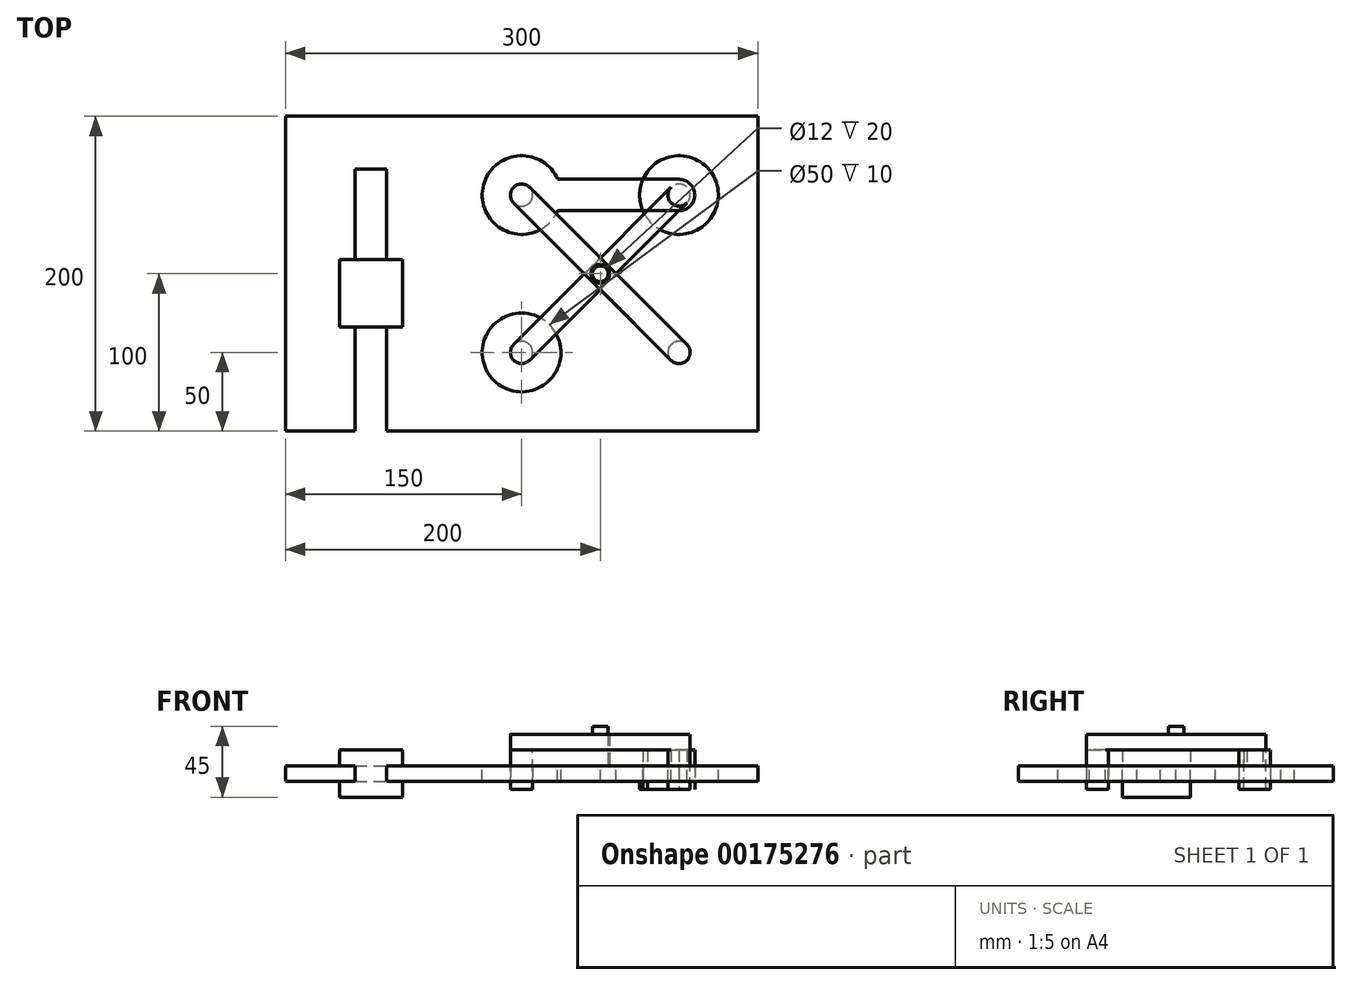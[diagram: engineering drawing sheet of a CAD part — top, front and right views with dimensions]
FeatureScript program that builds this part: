
annotation { "Feature Type Name" : "Feature", "Feature Type Description" : "" }
export const myFeature = defineFeature(function(context is Context, id is Id, definition is map)
    precondition{}
    {
        {
            var Q0;
            Q0=qCreatedBy(makeId("Top.planeOp"),FACE);
            var sketch = newSketch(context, id + "F0", { "sketchPlane" : qUnion([Q0])});
            skLineSegment(sketch, "E0.bottom", {"start": v(0, 0) * mm, "end": v(200, 0) * mm});
            skLineSegment(sketch, "E0.top", {"start": v(0, 200) * mm, "end": v(200, 200) * mm});
            skLineSegment(sketch, "E0.left", {"start": v(0, 0) * mm, "end": v(0, 200) * mm});
            skLineSegment(sketch, "E0.right", {"start": v(200, 0) * mm, "end": v(200, 200) * mm});
            skLineSegment(sketch, "E1", {"start": v(100, 200) * mm, "end": v(100, 0) * mm, "construction": true});
            skLineSegment(sketch, "E2", {"start": v(50, 200) * mm, "end": v(50, 0) * mm, "construction": true});
            skLineSegment(sketch, "E3.MirrorCS", {"start": v(150, 200) * mm, "end": v(150, 0) * mm, "construction": true});
            skLineSegment(sketch, "E4", {"start": v(0, 100) * mm, "end": v(200, 100) * mm, "construction": true});
            skLineSegment(sketch, "E5", {"start": v(0, 50) * mm, "end": v(200, 50) * mm, "construction": true});
            skLineSegment(sketch, "E6.MirrorCS", {"start": v(0, 150) * mm, "end": v(200, 150) * mm, "construction": true});
            skCircle(sketch, "E7", {"center": v(50, 50) * mm, "radius": 7.07 * mm});
            skCircle(sketch, "E8", {"center": v(150, 50) * mm, "radius": 7.07 * mm});
            skCircle(sketch, "E9", {"center": v(100, 100) * mm, "radius": 6 * mm});
            skCircle(sketch, "E10.MirrorC", {"center": v(50, 150) * mm, "radius": 7.07 * mm});
            skCircle(sketch, "E11.MirrorC", {"center": v(150, 150) * mm, "radius": 7.07 * mm});
            skLineSegment(sketch, "E12.bottom", {"start": v(55, 155) * mm, "end": v(45, 155) * mm, "construction": true});
            skLineSegment(sketch, "E12.top", {"start": v(55, 145) * mm, "end": v(45, 145) * mm, "construction": true});
            skLineSegment(sketch, "E12.left", {"start": v(55, 155) * mm, "end": v(55, 145) * mm, "construction": true});
            skLineSegment(sketch, "E12.right", {"start": v(45, 155) * mm, "end": v(45, 145) * mm, "construction": true});
            skLineSegment(sketch, "E13.bottom", {"start": v(155, 155) * mm, "end": v(145, 155) * mm, "construction": true});
            skLineSegment(sketch, "E13.top", {"start": v(155, 145) * mm, "end": v(145, 145) * mm, "construction": true});
            skLineSegment(sketch, "E13.left", {"start": v(155, 155) * mm, "end": v(155, 145) * mm, "construction": true});
            skLineSegment(sketch, "E13.right", {"start": v(145, 155) * mm, "end": v(145, 145) * mm, "construction": true});
            skLineSegment(sketch, "E14.bottom", {"start": v(105, 105) * mm, "end": v(95, 105) * mm, "construction": true});
            skLineSegment(sketch, "E14.top", {"start": v(105, 95) * mm, "end": v(95, 95) * mm, "construction": true});
            skLineSegment(sketch, "E14.left", {"start": v(105, 105) * mm, "end": v(105, 95) * mm, "construction": true});
            skLineSegment(sketch, "E14.right", {"start": v(95, 105) * mm, "end": v(95, 95) * mm, "construction": true});
            skLineSegment(sketch, "E15.bottom", {"start": v(55, 55) * mm, "end": v(45, 55) * mm, "construction": true});
            skLineSegment(sketch, "E15.top", {"start": v(55, 45) * mm, "end": v(45, 45) * mm, "construction": true});
            skLineSegment(sketch, "E15.left", {"start": v(55, 55) * mm, "end": v(55, 45) * mm, "construction": true});
            skLineSegment(sketch, "E15.right", {"start": v(45, 55) * mm, "end": v(45, 45) * mm, "construction": true});
            skLineSegment(sketch, "E16.bottom", {"start": v(155, 55) * mm, "end": v(145, 55) * mm, "construction": true});
            skLineSegment(sketch, "E16.top", {"start": v(155, 45) * mm, "end": v(145, 45) * mm, "construction": true});
            skLineSegment(sketch, "E16.left", {"start": v(155, 55) * mm, "end": v(155, 45) * mm, "construction": true});
            skLineSegment(sketch, "E16.right", {"start": v(145, 55) * mm, "end": v(145, 45) * mm, "construction": true});
            skCircle(sketch, "E17", {"center": v(50, 50) * mm, "radius": 25 * mm});
            skCircle(sketch, "E18.MirrorC", {"center": v(150, 50) * mm, "radius": 25 * mm});
            skLineSegment(sketch, "E19", {"start": v(155, 145) * mm, "end": v(145, 155) * mm, "construction": true});
            skLineSegment(sketch, "E20", {"start": v(155, 155) * mm, "end": v(145, 145) * mm, "construction": true});
            skLineSegment(sketch, "E21", {"start": v(55, 45) * mm, "end": v(45, 55) * mm, "construction": true});
            skLineSegment(sketch, "E22", {"start": v(55, 55) * mm, "end": v(45, 45) * mm, "construction": true});
            skLineSegment(sketch, "E23", {"start": v(145, 155) * mm, "end": v(45, 55) * mm});
            skLineSegment(sketch, "E24", {"start": v(55, 45) * mm, "end": v(155, 145) * mm});
            skLineSegment(sketch, "E25", {"start": v(155, 55) * mm, "end": v(55, 155) * mm});
            skLineSegment(sketch, "E26", {"start": v(45, 145) * mm, "end": v(145, 45) * mm});
            skCircle(sketch, "E27", {"center": v(100, 100) * mm, "radius": 5 * mm});
            skLineSegment(sketch, "E28", {"start": v(50, 150) * mm, "end": v(150, 150) * mm, "construction": true});
            skArc(sketch, "E29.0.startCap", {"start": v(50, 140) * mm, "mid": v(40, 150) * mm, "end": v(50, 160) * mm});
            skArc(sketch, "E29.0.endCap", {"start": v(150, 160) * mm, "mid": v(160, 150) * mm, "end": v(150, 140) * mm});
            skLineSegment(sketch, "E29.0.left", {"start": v(50, 160) * mm, "end": v(150, 160) * mm});
            skLineSegment(sketch, "E29.0.right", {"start": v(50, 140) * mm, "end": v(150, 140) * mm});
            skLineSegment(sketch, "E30.bottom", {"start": v(0, 0) * mm, "end": v(-100, 0) * mm});
            skLineSegment(sketch, "E30.top", {"start": v(0, 200) * mm, "end": v(-100, 200) * mm});
            skLineSegment(sketch, "E30.right", {"start": v(-100, 0) * mm, "end": v(-100, 200) * mm});
            skLineSegment(sketch, "E31", {"start": v(-45.65, 50) * mm, "end": v(-45.65, 150) * mm, "construction": true});
            skArc(sketch, "E32.0.startCap", {"start": v(-35.65, 50) * mm, "mid": v(-45.65, 40) * mm, "end": v(-55.65, 50) * mm});
            skArc(sketch, "E32.0.endCap", {"start": v(-55.65, 150) * mm, "mid": v(-45.65, 160) * mm, "end": v(-35.65, 150) * mm});
            skLineSegment(sketch, "E32.0.left", {"start": v(-55.65, 50) * mm, "end": v(-55.65, 150) * mm});
            skLineSegment(sketch, "E32.0.right", {"start": v(-35.65, 50) * mm, "end": v(-35.65, 150) * mm});
            skCircle(sketch, "E33", {"center": v(-45.65, 100) * mm, "radius": 9 * mm});
            skLineSegment(sketch, "E34.bottom", {"start": v(-65.65, 91) * mm, "end": v(-25.65, 91) * mm});
            skLineSegment(sketch, "E34.top", {"start": v(-65.65, 109) * mm, "end": v(-25.65, 109) * mm});
            skLineSegment(sketch, "E34.left", {"start": v(-65.65, 91) * mm, "end": v(-65.65, 109) * mm});
            skLineSegment(sketch, "E34.right", {"start": v(-25.65, 91) * mm, "end": v(-25.65, 109) * mm});
            skLineSegment(sketch, "E35", {"start": v(-35.65, 50) * mm, "end": v(-35.65, 0) * mm});
            skLineSegment(sketch, "E36", {"start": v(-55.65, 50) * mm, "end": v(-55.65, 0) * mm});
            skLineSegment(sketch, "E37.bottom", {"start": v(-55.65, 150) * mm, "end": v(-35.65, 150) * mm});
            skLineSegment(sketch, "E37.top", {"start": v(-55.65, 166.53) * mm, "end": v(-35.65, 166.53) * mm});
            skLineSegment(sketch, "E37.left", {"start": v(-55.65, 150) * mm, "end": v(-55.65, 166.53) * mm});
            skLineSegment(sketch, "E37.right", {"start": v(-35.65, 150) * mm, "end": v(-35.65, 166.53) * mm});
            skCircle(sketch, "E38.MirrorC", {"center": v(50, 150) * mm, "radius": 25 * mm});
            skCircle(sketch, "E39.MirrorC", {"center": v(150, 150) * mm, "radius": 25 * mm});
            skSolve(sketch);
        }
        {
            var Q0;
            Q0=makeQuery(id+"F0.imprint","IMPRINT",FACE,{"disambiguationData":[TD([[makeQuery(id+"F0.imprint","IMPRINT",EDGE,{"derivedFrom":sQuery(id+"F0.wireOp",EDGE,"E9")}),-1.0]])]});
            var Q1;
            Q1=makeQuery(id+"F0.imprint","IMPRINT",FACE,{"disambiguationData":[TD([[makeQuery(id+"F0.imprint","IMPRINT",EDGE,{"derivedFrom":sQuery(id+"F0.wireOp",EDGE,"E27")}),1.0]])]});
            var Q2;
            Q2=makeQuery(id+"F0.imprint","IMPRINT",FACE,{"disambiguationData":[TD([[makeQuery(id+"F0.imprint","IMPRINT",EDGE,{"derivedFrom":sQuery(id+"F0.wireOp",EDGE,"E9")}),1.0]])]});
            var Q3;
            {var subQ0=sQuery(id+"F0.wireOp",EDGE,"E25");var subQ1=sQuery(id+"F0.wireOp",EDGE,"E18.MirrorC");var subQ2=makeQuery(id+"F0.imprint","INTERSECT",VERTEX,{"derivedFrom":[subQ1,subQ0]});Q3=makeQuery(id+"F0.imprint","IMPRINT",FACE,{"disambiguationData":[TD([[makeQuery(id+"F0.imprint","IMPRINT",EDGE,{"disambiguationData":[TD([[subQ2,1.0]])],"derivedFrom":subQ1}),1.0]])]});}
            var Q4;
            {var subQ0=sQuery(id+"F0.wireOp",EDGE,"E23");var subQ1=sQuery(id+"F0.wireOp",EDGE,"E17");var subQ2=makeQuery(id+"F0.imprint","INTERSECT",VERTEX,{"derivedFrom":[subQ1,subQ0]});Q4=makeQuery(id+"F0.imprint","IMPRINT",FACE,{"disambiguationData":[TD([[makeQuery(id+"F0.imprint","IMPRINT",EDGE,{"disambiguationData":[TD([[subQ2,1.0]])],"derivedFrom":subQ1}),-1.0]])]});}
            var Q5;
            {var subQ0=sQuery(id+"F0.wireOp",EDGE,"E25");var subQ1=sQuery(id+"F0.wireOp",EDGE,"E23");var subQ2=makeQuery(id+"F0.imprint","INTERSECT",VERTEX,{"derivedFrom":[subQ1,subQ0]});Q5=makeQuery(id+"F0.imprint","IMPRINT",FACE,{"disambiguationData":[TD([[makeQuery(id+"F0.imprint","IMPRINT",EDGE,{"disambiguationData":[TD([[subQ2,-1.0]])],"derivedFrom":subQ1}),-1.0]])]});}
            var Q6;
            Q6=makeQuery(id+"F0.imprint","IMPRINT",FACE,{"disambiguationData":[TD([[makeQuery(id+"F0.imprint","IMPRINT",EDGE,{"derivedFrom":sQuery(id+"F0.wireOp",EDGE,"E30.bottom")}),-1.0]])]});
            var Q7;
            {var subQ5=sQuery(id+"F0.wireOp",EDGE,"E34.right");Q7=makeQuery(id+"F0.imprint","IMPRINT",FACE,{"disambiguationData":[TD([[makeQuery(id+"F0.imprint","IMPRINT",EDGE,{"derivedFrom":subQ5}),1.0]])]});}
            var Q8;
            {var subQ5=sQuery(id+"F0.wireOp",EDGE,"E34.left");Q8=makeQuery(id+"F0.imprint","IMPRINT",FACE,{"disambiguationData":[TD([[makeQuery(id+"F0.imprint","IMPRINT",EDGE,{"derivedFrom":subQ5}),-1.0]])]});}
            var Q9;
            Q9=makeQuery(id+"F0.imprint","IMPRINT",FACE,{"disambiguationData":[TD([[makeQuery(id+"F0.imprint","IMPRINT",EDGE,{"derivedFrom":sQuery(id+"F0.wireOp",EDGE,"E0.bottom")}),1.0]])]});
            var Q10;
            {var subQ1=sQuery(id+"F0.wireOp",EDGE,"E23");var subQ7=sQuery(id+"F0.wireOp",EDGE,"E39.MirrorC");var subQ9=makeQuery(id+"F0.imprint","INTERSECT",VERTEX,{"derivedFrom":[subQ1,subQ7]});Q10=makeQuery(id+"F0.imprint","IMPRINT",FACE,{"disambiguationData":[TD([[makeQuery(id+"F0.imprint","IMPRINT",EDGE,{"disambiguationData":[TD([[subQ9,-1.0]])],"derivedFrom":subQ1}),-1.0]])]});}
            var Q11;
            {var subQ0=sQuery(id+"F0.wireOp",EDGE,"E39.MirrorC");var subQ1=sQuery(id+"F0.wireOp",EDGE,"E23");var subQ2=makeQuery(id+"F0.imprint","INTERSECT",VERTEX,{"derivedFrom":[subQ1,subQ0]});Q11=makeQuery(id+"F0.imprint","IMPRINT",FACE,{"disambiguationData":[TD([[makeQuery(id+"F0.imprint","IMPRINT",EDGE,{"disambiguationData":[TD([[subQ2,-1.0]])],"derivedFrom":subQ1}),1.0]])]});}
            extrude(context, id + "F1", {"entities" : qUnion([Q0, Q1, Q2, Q3, Q4, Q5, Q6, Q7, Q8, Q9, Q10, Q11]), "oppositeDirection" : true, "depth" : 10 * mm});
        }
        {
            var Q0;
            Q0=makeQuery(id+"F0.imprint","IMPRINT",FACE,{"disambiguationData":[TD([[makeQuery(id+"F0.imprint","IMPRINT",EDGE,{"derivedFrom":sQuery(id+"F0.wireOp",EDGE,"E27")}),1.0]])]});
            extrude(context, id + "F2", {"entities" : qUnion([Q0]), "operationType" : NewBodyOperationType.ADD, "depth" : 25 * mm});
        }
        {
            var Q0;
            {var subQ0=sQuery(id+"F0.wireOp",EDGE,"E23");var subQ1=sQuery(id+"F0.wireOp",EDGE,"E17");var subQ2=makeQuery(id+"F0.imprint","INTERSECT",VERTEX,{"derivedFrom":[subQ1,subQ0]});Q0=makeQuery(id+"F0.imprint","IMPRINT",FACE,{"disambiguationData":[TD([[makeQuery(id+"F0.imprint","IMPRINT",EDGE,{"disambiguationData":[TD([[subQ2,1.0]])],"derivedFrom":subQ1}),-1.0]])]});}
            var Q1;
            Q1=makeQuery(id+"F0.imprint","IMPRINT",FACE,{"disambiguationData":[TD([[makeQuery(id+"F0.imprint","IMPRINT",EDGE,{"derivedFrom":sQuery(id+"F0.wireOp",EDGE,"E9")}),-1.0]])]});
            var Q2;
            {var subQ0=sQuery(id+"F0.wireOp",EDGE,"E29.0.right");var subQ1=sQuery(id+"F0.wireOp",EDGE,"E23");var subQ2=makeQuery(id+"F0.imprint","INTERSECT",VERTEX,{"derivedFrom":[subQ1,subQ0]});Q2=makeQuery(id+"F0.imprint","IMPRINT",FACE,{"disambiguationData":[TD([[makeQuery(id+"F0.imprint","IMPRINT",EDGE,{"disambiguationData":[TD([[subQ2,-1.0]])],"derivedFrom":subQ1}),1.0]])]});}
            var Q3;
            {var subQ0=sQuery(id+"F0.wireOp",EDGE,"E23");var subQ1=sQuery(id+"F0.wireOp",EDGE,"E11.MirrorC");var subQ2=makeQuery(id+"F0.imprint","INTERSECT",VERTEX,{"derivedFrom":[subQ1,subQ0]});Q3=makeQuery(id+"F0.imprint","IMPRINT",FACE,{"disambiguationData":[TD([[makeQuery(id+"F0.imprint","IMPRINT",EDGE,{"disambiguationData":[TD([[subQ2,1.0]])],"derivedFrom":subQ1}),1.0]])]});}
            var Q4;
            {var subQ0=sQuery(id+"F0.wireOp",EDGE,"E11.MirrorC");var subQ1=makeQuery(id+"F0.imprint","INTERSECT",VERTEX,{"derivedFrom":[subQ0,sQuery(id+"F0.wireOp",EDGE,"E23")]});Q4=makeQuery(id+"F0.imprint","IMPRINT",FACE,{"disambiguationData":[TD([[makeQuery(id+"F0.imprint","IMPRINT",EDGE,{"disambiguationData":[TD([[subQ1,1.0]])],"derivedFrom":subQ0}),-1.0]])]});}
            var Q5;
            {var subQ0=sQuery(id+"F0.wireOp",EDGE,"E23");var subQ1=sQuery(id+"F0.wireOp",EDGE,"E7");var subQ2=makeQuery(id+"F0.imprint","INTERSECT",VERTEX,{"derivedFrom":[subQ1,subQ0]});Q5=makeQuery(id+"F0.imprint","IMPRINT",FACE,{"disambiguationData":[TD([[makeQuery(id+"F0.imprint","IMPRINT",EDGE,{"disambiguationData":[TD([[subQ2,1.0]])],"derivedFrom":subQ1}),-1.0]])]});}
            var Q6;
            {var subQ0=sQuery(id+"F0.wireOp",EDGE,"E7");var subQ1=makeQuery(id+"F0.imprint","INTERSECT",VERTEX,{"derivedFrom":[subQ0,sQuery(id+"F0.wireOp",EDGE,"E23")]});Q6=makeQuery(id+"F0.imprint","IMPRINT",FACE,{"disambiguationData":[TD([[makeQuery(id+"F0.imprint","IMPRINT",EDGE,{"disambiguationData":[TD([[subQ1,-1.0]])],"derivedFrom":subQ0}),1.0]])]});}
            var Q7;
            {var subQ0=sQuery(id+"F0.wireOp",EDGE,"E39.MirrorC");var subQ1=sQuery(id+"F0.wireOp",EDGE,"E23");var subQ2=makeQuery(id+"F0.imprint","INTERSECT",VERTEX,{"derivedFrom":[subQ1,subQ0]});Q7=makeQuery(id+"F0.imprint","IMPRINT",FACE,{"disambiguationData":[TD([[makeQuery(id+"F0.imprint","IMPRINT",EDGE,{"disambiguationData":[TD([[subQ2,-1.0]])],"derivedFrom":subQ1}),1.0]])]});}
            extrude(context, id + "F3", {"entities" : qUnion([Q0, Q1, Q2, Q3, Q4, Q5, Q6, Q7]), "depth" : 10 * mm});
        }
        {
            var Q0;
            Q0=qCreatedBy(makeId("Top.planeOp"),FACE);
            cPlane(context, id + "F4", {"entities" : qUnion([Q0]), "cplaneType" : CPlaneType.OFFSET, "offset" : 20 * mm, "width" : 150 * mm, "height" : 150 * mm});
        }
        {
            var Q0;
            Q0=qCreatedBy(id+"F4.planeOp",FACE);
            var sketch = newSketch(context, id + "F5", { "sketchPlane" : qUnion([Q0])});
            skLineSegment(sketch, "E40", {"start": v(155, 55) * mm, "end": v(55, 155) * mm});
            skLineSegment(sketch, "E41", {"start": v(145, 45) * mm, "end": v(45, 145) * mm});
            skCircle(sketch, "E42", {"center": v(50, 150) * mm, "radius": 7.07 * mm});
            skCircle(sketch, "E43", {"center": v(150, 50) * mm, "radius": 7.07 * mm});
            skCircle(sketch, "E44", {"center": v(100, 100) * mm, "radius": 6 * mm});
            skSolve(sketch);
        }
        {
            var Q0;
            {var subQ0=sQuery(id+"F5.wireOp",EDGE,"E42");var subQ1=makeQuery(id+"F5.imprint","INTERSECT",VERTEX,{"derivedFrom":[sQuery(id+"F5.wireOp",EDGE,"E40"),subQ0]});Q0=makeQuery(id+"F5.imprint","IMPRINT",FACE,{"disambiguationData":[TD([[makeQuery(id+"F5.imprint","IMPRINT",EDGE,{"disambiguationData":[TD([[subQ1,-1.0]])],"derivedFrom":subQ0}),1.0]])]});}
            var Q1;
            {var subQ0=sQuery(id+"F5.wireOp",EDGE,"E43");var subQ1=makeQuery(id+"F5.imprint","INTERSECT",VERTEX,{"derivedFrom":[sQuery(id+"F5.wireOp",EDGE,"E40"),subQ0]});Q1=makeQuery(id+"F5.imprint","IMPRINT",FACE,{"disambiguationData":[TD([[makeQuery(id+"F5.imprint","IMPRINT",EDGE,{"disambiguationData":[TD([[subQ1,-1.0]])],"derivedFrom":subQ0}),1.0]])]});}
            var Q2;
            {var subQ0=sQuery(id+"F5.wireOp",EDGE,"E40");Q2=makeQuery(id+"F5.imprint","IMPRINT",FACE,{"disambiguationData":[TD([[makeQuery(id+"F5.imprint","IMPRINT",EDGE,{"derivedFrom":subQ0}),1.0]])]});}
            extrude(context, id + "F6", {"entities" : qUnion([Q0, Q1, Q2]), "oppositeDirection" : true, "depth" : 10 * mm});
        }
        {
            var Q0;
            {var subQ0=sQuery(id+"F0.wireOp",EDGE,"E7");var subQ1=makeQuery(id+"F0.imprint","INTERSECT",VERTEX,{"derivedFrom":[subQ0,sQuery(id+"F0.wireOp",EDGE,"E23")]});Q0=makeQuery(id+"F0.imprint","IMPRINT",FACE,{"disambiguationData":[TD([[makeQuery(id+"F0.imprint","IMPRINT",EDGE,{"disambiguationData":[TD([[subQ1,-1.0]])],"derivedFrom":subQ0}),1.0]])]});}
            var Q1;
            {var subQ0=sQuery(id+"F0.wireOp",EDGE,"E11.MirrorC");var subQ1=makeQuery(id+"F0.imprint","INTERSECT",VERTEX,{"derivedFrom":[subQ0,sQuery(id+"F0.wireOp",EDGE,"E23")]});Q1=makeQuery(id+"F0.imprint","IMPRINT",FACE,{"disambiguationData":[TD([[makeQuery(id+"F0.imprint","IMPRINT",EDGE,{"disambiguationData":[TD([[subQ1,1.0]])],"derivedFrom":subQ0}),-1.0]])]});}
            var Q2;
            Q2=sQuery(id+"F0.wireOp",EDGE,"E7");
            extrude(context, id + "F7", {"entities" : qUnion([Q0, Q1]), "operationType" : NewBodyOperationType.ADD, "surfaceEntities" : qUnion([Q2]), "oppositeDirection" : true, "depth" : 15 * mm});
        }
        {
            var Q0;
            {var subQ0=sQuery(id+"F5.wireOp",EDGE,"E42");var subQ1=makeQuery(id+"F5.imprint","INTERSECT",VERTEX,{"derivedFrom":[sQuery(id+"F5.wireOp",EDGE,"E40"),subQ0]});Q0=makeQuery(id+"F5.imprint","IMPRINT",FACE,{"disambiguationData":[TD([[makeQuery(id+"F5.imprint","IMPRINT",EDGE,{"disambiguationData":[TD([[subQ1,-1.0]])],"derivedFrom":subQ0}),1.0]])]});}
            var Q1;
            {var subQ0=sQuery(id+"F5.wireOp",EDGE,"E43");var subQ1=makeQuery(id+"F5.imprint","INTERSECT",VERTEX,{"derivedFrom":[sQuery(id+"F5.wireOp",EDGE,"E40"),subQ0]});Q1=makeQuery(id+"F5.imprint","IMPRINT",FACE,{"disambiguationData":[TD([[makeQuery(id+"F5.imprint","IMPRINT",EDGE,{"disambiguationData":[TD([[subQ1,-1.0]])],"derivedFrom":subQ0}),1.0]])]});}
            var Q2;
            Q2=sQuery(id+"F5.wireOp",EDGE,"E43");
            var Q3;
            Q3=sQuery(id+"F5.wireOp",EDGE,"E42");
            extrude(context, id + "F8", {"entities" : qUnion([Q0, Q1]), "operationType" : NewBodyOperationType.ADD, "surfaceEntities" : qUnion([Q2, Q3]), "oppositeDirection" : true, "depth" : 35 * mm});
        }
        {
            var Q0;
            {var subQ0=sQuery(id+"F0.wireOp",EDGE,"E33");var subQ1=makeQuery(id+"F0.imprint","INTERSECT",VERTEX,{"derivedFrom":[subQ0,sQuery(id+"F0.wireOp",EDGE,"E34.bottom")]});Q0=makeQuery(id+"F0.imprint","IMPRINT",FACE,{"disambiguationData":[TD([[makeQuery(id+"F0.imprint","IMPRINT",EDGE,{"disambiguationData":[TD([[subQ1,1.0]])],"derivedFrom":subQ0}),1.0]])]});}
            var Q1;
            {var subQ5=sQuery(id+"F0.wireOp",EDGE,"E34.right");Q1=makeQuery(id+"F0.imprint","IMPRINT",FACE,{"disambiguationData":[TD([[makeQuery(id+"F0.imprint","IMPRINT",EDGE,{"derivedFrom":subQ5}),1.0]])]});}
            var Q2;
            {var subQ0=sQuery(id+"F0.wireOp",EDGE,"E34.bottom");var subQ1=sQuery(id+"F0.wireOp",EDGE,"E32.0.right");var subQ2=makeQuery(id+"F0.imprint","INTERSECT",VERTEX,{"derivedFrom":[subQ1,subQ0]});Q2=makeQuery(id+"F0.imprint","IMPRINT",FACE,{"disambiguationData":[TD([[makeQuery(id+"F0.imprint","IMPRINT",EDGE,{"disambiguationData":[TD([[subQ2,-1.0]])],"derivedFrom":subQ1}),1.0]])]});}
            var Q3;
            {var subQ0=sQuery(id+"F0.wireOp",EDGE,"E34.bottom");var subQ1=sQuery(id+"F0.wireOp",EDGE,"E32.0.left");var subQ2=makeQuery(id+"F0.imprint","INTERSECT",VERTEX,{"derivedFrom":[subQ1,subQ0]});Q3=makeQuery(id+"F0.imprint","IMPRINT",FACE,{"disambiguationData":[TD([[makeQuery(id+"F0.imprint","IMPRINT",EDGE,{"disambiguationData":[TD([[subQ2,-1.0]])],"derivedFrom":subQ1}),-1.0]])]});}
            var Q4;
            {var subQ5=sQuery(id+"F0.wireOp",EDGE,"E34.left");Q4=makeQuery(id+"F0.imprint","IMPRINT",FACE,{"disambiguationData":[TD([[makeQuery(id+"F0.imprint","IMPRINT",EDGE,{"derivedFrom":subQ5}),-1.0]])]});}
            extrude(context, id + "F9", {"entities" : qUnion([Q0, Q1, Q2, Q3, Q4]), "depth" : 10 * mm});
        }
        {
            var Q0;
            {var subQ0=sQuery(id+"F0.wireOp",EDGE,"E33");var subQ1=makeQuery(id+"F0.imprint","INTERSECT",VERTEX,{"derivedFrom":[subQ0,sQuery(id+"F0.wireOp",EDGE,"E34.bottom")]});Q0=makeQuery(id+"F0.imprint","IMPRINT",FACE,{"disambiguationData":[TD([[makeQuery(id+"F0.imprint","IMPRINT",EDGE,{"disambiguationData":[TD([[subQ1,1.0]])],"derivedFrom":subQ0}),1.0]])]});}
            var Q1;
            {var subQ0=sQuery(id+"F0.wireOp",EDGE,"E34.bottom");var subQ1=sQuery(id+"F0.wireOp",EDGE,"E32.0.right");var subQ2=makeQuery(id+"F0.imprint","INTERSECT",VERTEX,{"derivedFrom":[subQ1,subQ0]});Q1=makeQuery(id+"F0.imprint","IMPRINT",FACE,{"disambiguationData":[TD([[makeQuery(id+"F0.imprint","IMPRINT",EDGE,{"disambiguationData":[TD([[subQ2,-1.0]])],"derivedFrom":subQ1}),1.0]])]});}
            var Q2;
            {var subQ0=sQuery(id+"F0.wireOp",EDGE,"E34.bottom");var subQ1=sQuery(id+"F0.wireOp",EDGE,"E32.0.left");var subQ2=makeQuery(id+"F0.imprint","INTERSECT",VERTEX,{"derivedFrom":[subQ1,subQ0]});Q2=makeQuery(id+"F0.imprint","IMPRINT",FACE,{"disambiguationData":[TD([[makeQuery(id+"F0.imprint","IMPRINT",EDGE,{"disambiguationData":[TD([[subQ2,-1.0]])],"derivedFrom":subQ1}),-1.0]])]});}
            extrude(context, id + "F10", {"entities" : qUnion([Q0, Q1, Q2]), "operationType" : NewBodyOperationType.ADD, "oppositeDirection" : true, "depth" : 10 * mm});
        }
        {
            var Q0;
            Q0=makeQuery(id+"F1.opExtrude","CAP_FACE",FACE,{"disambiguationData":[OSD([sQuery(id+"F0.wireOp",EDGE,"E0.bottom"),sQuery(id+"F0.wireOp",EDGE,"E0.top"),sQuery(id+"F0.wireOp",EDGE,"E0.right"),sQuery(id+"F0.wireOp",EDGE,"E17"),sQuery(id+"F0.wireOp",EDGE,"E18.MirrorC"),sQuery(id+"F0.wireOp",EDGE,"E29.0.startCap"),sQuery(id+"F0.wireOp",EDGE,"E29.0.endCap"),sQuery(id+"F0.wireOp",EDGE,"E29.0.left"),sQuery(id+"F0.wireOp",EDGE,"E29.0.right"),sQuery(id+"F0.wireOp",EDGE,"E30.bottom"),sQuery(id+"F0.wireOp",EDGE,"E30.top"),sQuery(id+"F0.wireOp",EDGE,"E30.right"),sQuery(id+"F0.wireOp",EDGE,"E32.0.endCap"),sQuery(id+"F0.wireOp",EDGE,"E32.0.left"),sQuery(id+"F0.wireOp",EDGE,"E32.0.right"),sQuery(id+"F0.wireOp",EDGE,"E35"),sQuery(id+"F0.wireOp",EDGE,"E36")])],"isStart":false});
            var sketch = newSketch(context, id + "F11", { "sketchPlane" : qUnion([Q0])});
            skLineSegment(sketch, "E45.bottom", {"start": v(-25.65, -109) * mm, "end": v(-65.65, -109) * mm});
            skLineSegment(sketch, "E45.top", {"start": v(-25.65, -91) * mm, "end": v(-65.65, -91) * mm});
            skLineSegment(sketch, "E45.left", {"start": v(-25.65, -109) * mm, "end": v(-25.65, -91) * mm});
            skLineSegment(sketch, "E45.right", {"start": v(-65.65, -109) * mm, "end": v(-65.65, -91) * mm});
            skPoint(sketch, "E45.middle", {"position": v(-45.65, -100) * mm});
            skSolve(sketch);
        }
        {
            var Q0;
            {var subQ0=sQuery(id+"F11.wireOp",EDGE,"E45.right");Q0=makeQuery(id+"F11.imprint","IMPRINT",FACE,{"disambiguationData":[TD([[makeQuery(id+"F11.imprint","IMPRINT",EDGE,{"derivedFrom":subQ0}),-1.0]])]});}
            var Q1;
            {var subQ0=sQuery(id+"F11.wireOp",EDGE,"E45.bottom");var subQ1=makeQuery(id+"F1.opExtrude","CAP_EDGE",EDGE,{"disambiguationData":[OSD([sQuery(id+"F0.wireOp",EDGE,"E32.0.right"),sQuery(id+"F0.wireOp",EDGE,"E35")])],"isStart":false});var subQ2=makeQuery(id+"F11.imprint","INTERSECT",VERTEX,{"derivedFrom":[subQ1,subQ0]});Q1=makeQuery(id+"F11.imprint","IMPRINT",FACE,{"disambiguationData":[TD([[makeQuery(id+"F11.imprint","IMPRINT",EDGE,{"disambiguationData":[TD([[subQ2,-1.0]])],"derivedFrom":subQ0}),-1.0]])]});}
            var Q2;
            {var subQ0=sQuery(id+"F11.wireOp",EDGE,"E45.left");Q2=makeQuery(id+"F11.imprint","IMPRINT",FACE,{"disambiguationData":[TD([[makeQuery(id+"F11.imprint","IMPRINT",EDGE,{"derivedFrom":subQ0}),1.0]])]});}
            extrude(context, id + "F12", {"entities" : qUnion([Q0, Q1, Q2]), "operationType" : NewBodyOperationType.ADD, "depth" : 10 * mm});
        }
        {
            var Q0;
            {var subQ0=sQuery(id+"F0.wireOp",EDGE,"E34.bottom");Q0=makeQuery(id+"F12.boolean.opBoolean","MERGE",FACE,{"derivedFrom":[makeQuery(id+"F10.boolean.opBoolean","MERGE",FACE,{"derivedFrom":[makeQuery(id+"F9.opExtrude","SWEPT_FACE",FACE,{"disambiguationData":[OSD([subQ0])]}),makeQuery(id+"F10.opExtrude","SWEPT_FACE",FACE,{"disambiguationData":[OSD([subQ0])]})]}),makeQuery(id+"F12.opExtrude","SWEPT_FACE",FACE,{"disambiguationData":[OSD([sQuery(id+"F11.wireOp",EDGE,"E45.top")])]})]});}
            extrude(context, id + "F13", {"entities" : qUnion([Q0]), "operationType" : NewBodyOperationType.ADD, "depth" : 25 * mm});
        }
    });
